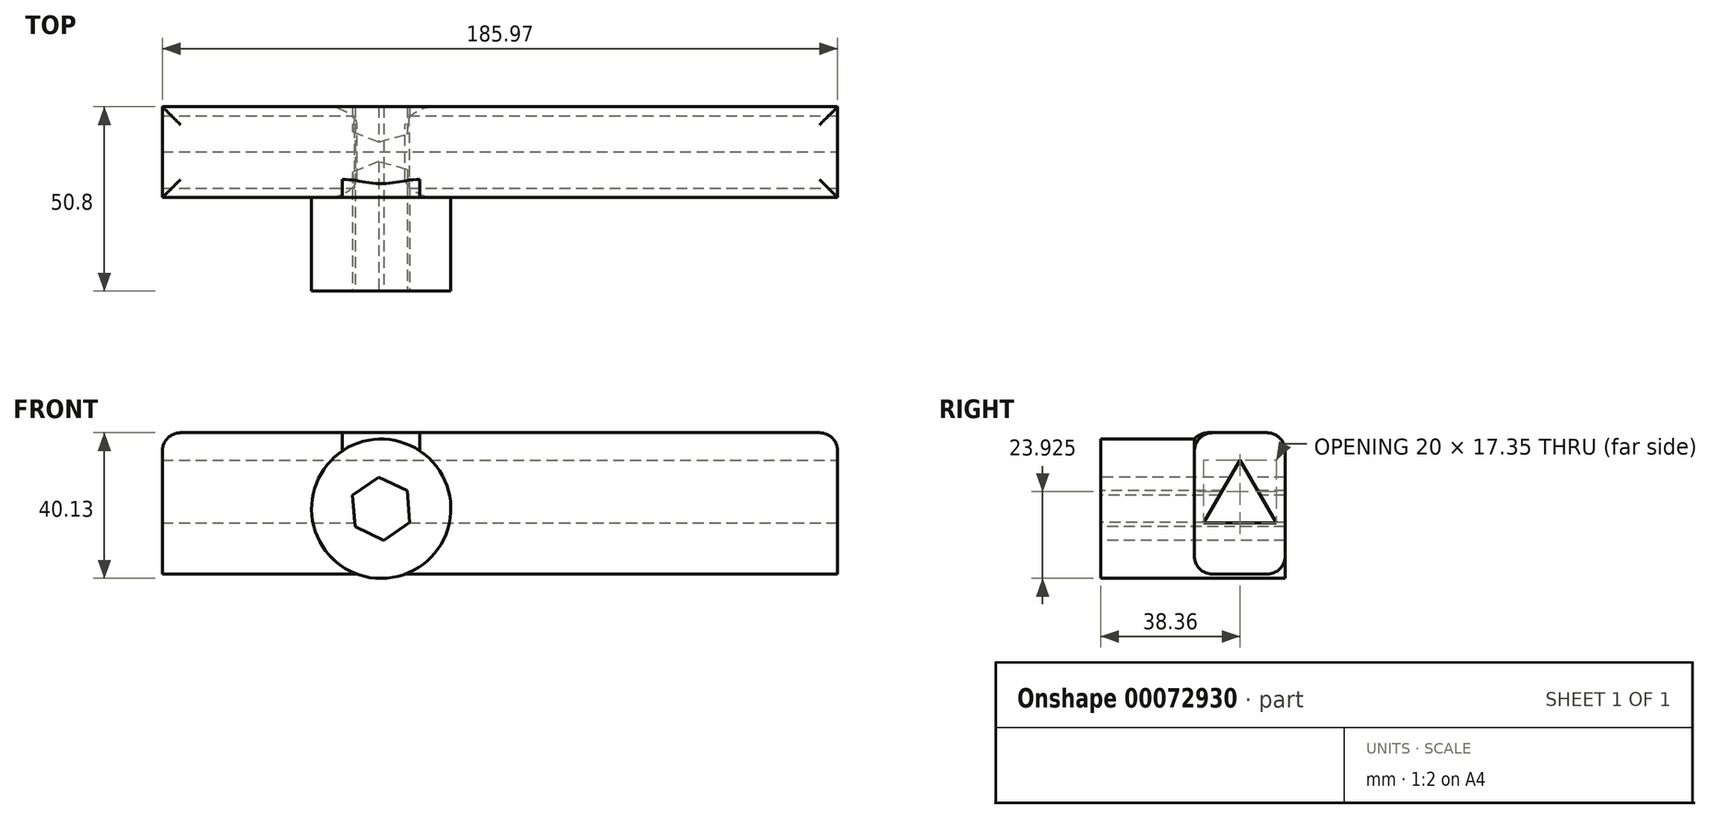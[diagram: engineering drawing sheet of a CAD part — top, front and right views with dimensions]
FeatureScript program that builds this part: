
annotation { "Feature Type Name" : "Feature", "Feature Type Description" : "" }
export const myFeature = defineFeature(function(context is Context, id is Id, definition is map)
    precondition{}
    {
        {
            var Q0;
            Q0=qCreatedBy(makeId("Front.planeOp"),FACE);
            var sketch = newSketch(context, id + "F0", { "sketchPlane" : qUnion([Q0])});
            skCircle(sketch, "E0", {"center": v(-60.55, 49.23) * mm, "radius": 19.19 * mm});
            skSolve(sketch);
        }
        {
            var Q0;
            Q0 = qSketchRegion(id + "F0", true);
            extrude(context, id + "F1", {"entities" : qUnion([Q0]), "depth" : 50.8 * mm});
        }
        {
            var Q0;
            Q0=qCreatedBy(makeId("Front.planeOp"),FACE);
            var sketch = newSketch(context, id + "F2", { "sketchPlane" : qUnion([Q0])});
            skLineSegment(sketch, "E1.bottom", {"start": v(-120.8, 70.18) * mm, "end": v(65.17, 70.18) * mm});
            skLineSegment(sketch, "E1.top", {"start": v(-120.8, 31.22) * mm, "end": v(65.17, 31.22) * mm});
            skLineSegment(sketch, "E1.left", {"start": v(-120.8, 70.18) * mm, "end": v(-120.8, 31.22) * mm});
            skLineSegment(sketch, "E1.right", {"start": v(65.17, 70.18) * mm, "end": v(65.17, 31.22) * mm});
            skSolve(sketch);
        }
        {
            var Q0;
            Q0=makeQuery(id+"F2.imprint","IMPRINT",FACE,{"disambiguationData":[TD([[makeQuery(id+"F2.imprint","IMPRINT",EDGE,{"derivedFrom":sQuery(id+"F2.wireOp",EDGE,"E1.bottom")}),-1.0]])]});
            extrude(context, id + "F3", {"entities" : qUnion([Q0]), "operationType" : NewBodyOperationType.ADD, "depth" : 25 * mm});
        }
        {
            var Q0;
            Q0=makeQuery(id+"F3.opExtrude","SWEPT_FACE",FACE,{"disambiguationData":[OSD([sQuery(id+"F2.wireOp",EDGE,"E1.bottom")])]});
            fillet(context, id + "F4", {"entities" : qUnion([Q0]), "radius" : 5 * mm, "tangentPropagation" : true, "allowEdgeOverflow" : false});
        }
        {
            var Q0;
            {var subQ0=sQuery(id+"F2.wireOp",EDGE,"E1.top");var subQ1=sQuery(id+"F2.wireOp",EDGE,"E1.right");Q0=makeQuery(id+"F3.boolean.opBoolean","SPLIT",EDGE,{"disambiguationData":[TD([makeQuery(id+"F3.opExtrude","SWEPT_FACE",FACE,{"disambiguationData":[OSD([subQ1])]})])],"derivedFrom":makeQuery(id+"F3.opExtrude","CAP_EDGE",EDGE,{"disambiguationData":[OSD([subQ0])],"isStart":true})});}
            fillet(context, id + "F5", {"entities" : qUnion([Q0]), "radius" : 5 * mm, "tangentPropagation" : true, "allowEdgeOverflow" : false});
        }
        {
            var Q0;
            {var subQ0=sQuery(id+"F2.wireOp",EDGE,"E1.top");var subQ1=sQuery(id+"F2.wireOp",EDGE,"E1.left");Q0=makeQuery(id+"F3.boolean.opBoolean","SPLIT",EDGE,{"disambiguationData":[TD([makeQuery(id+"F3.opExtrude","SWEPT_FACE",FACE,{"disambiguationData":[OSD([subQ1])]})])],"derivedFrom":makeQuery(id+"F3.opExtrude","CAP_EDGE",EDGE,{"disambiguationData":[OSD([subQ0])],"isStart":true})});}
            fillet(context, id + "F6", {"entities" : qUnion([Q0]), "radius" : 5 * mm, "tangentPropagation" : true, "allowEdgeOverflow" : false});
        }
        {
            var Q0;
            {var subQ0=sQuery(id+"F2.wireOp",EDGE,"E1.left");var subQ1=sQuery(id+"F2.wireOp",EDGE,"E1.top");Q0=makeQuery(id+"F3.boolean.opBoolean","SPLIT",EDGE,{"disambiguationData":[TD([makeQuery(id+"F3.opExtrude","SWEPT_FACE",FACE,{"disambiguationData":[OSD([subQ0])]})])],"derivedFrom":makeQuery(id+"F3.opExtrude","CAP_EDGE",EDGE,{"disambiguationData":[OSD([subQ1])],"isStart":false})});}
            var Q1;
            {var subQ0=sQuery(id+"F2.wireOp",EDGE,"E1.right");var subQ1=sQuery(id+"F2.wireOp",EDGE,"E1.top");Q1=makeQuery(id+"F3.boolean.opBoolean","SPLIT",EDGE,{"disambiguationData":[TD([makeQuery(id+"F3.opExtrude","SWEPT_FACE",FACE,{"disambiguationData":[OSD([subQ0])]})])],"derivedFrom":makeQuery(id+"F3.opExtrude","CAP_EDGE",EDGE,{"disambiguationData":[OSD([subQ1])],"isStart":false})});}
            fillet(context, id + "F7", {"entities" : qUnion([Q0, Q1]), "radius" : 5 * mm, "tangentPropagation" : true, "allowEdgeOverflow" : false});
        }
        {
            var Q0;
            Q0=makeQuery(id+"F3.opExtrude","SWEPT_FACE",FACE,{"disambiguationData":[OSD([sQuery(id+"F2.wireOp",EDGE,"E1.right")])]});
            var sketch = newSketch(context, id + "F8", { "sketchPlane" : qUnion([Q0])});
            skCircle(sketch, "E2.cCircle", {"center": v(-12.42, 51.1) * mm, "radius": 5.77 * mm, "construction": true});
            skLineSegment(sketch, "E2.0", {"start": v(-2.44, 45.3) * mm, "end": v(-22.44, 45.36) * mm});
            skLineSegment(sketch, "E2.1", {"start": v(-22.44, 45.36) * mm, "end": v(-12.4, 62.65) * mm});
            skLineSegment(sketch, "E2.2", {"start": v(-12.4, 62.65) * mm, "end": v(-2.44, 45.3) * mm});
            skPoint(sketch, "E2.0.midPoint", {"position": v(-12.44, 45.33) * mm});
            skSolve(sketch);
        }
        {
            var Q0;
            Q0=makeQuery(id+"F8.imprint","IMPRINT",FACE,{"disambiguationData":[TD([[makeQuery(id+"F8.imprint","IMPRINT",EDGE,{"derivedFrom":sQuery(id+"F8.wireOp",EDGE,"E2.0")}),-1.0]])]});
            extrude(context, id + "F9", {"entities" : qUnion([Q0]), "operationType" : NewBodyOperationType.REMOVE, "endBound" : BoundingType.THROUGH_ALL, "oppositeDirection" : true, "depth" : 25 * mm});
        }
        {
            var Q0;
            Q0=makeQuery(id+"F1.opExtrude","CAP_FACE",FACE,{"disambiguationData":[OSD([sQuery(id+"F0.wireOp",EDGE,"E0")])],"isStart":false});
            var sketch = newSketch(context, id + "F10", { "sketchPlane" : qUnion([Q0])});
            skCircle(sketch, "E3.cCircle", {"center": v(-60.55, 49.23) * mm, "radius": 7.57 * mm, "construction": true});
            skLineSegment(sketch, "E3.0", {"start": v(-52.66, 45.48) * mm, "end": v(-59.86, 40.52) * mm});
            skLineSegment(sketch, "E3.1", {"start": v(-59.86, 40.52) * mm, "end": v(-67.75, 44.28) * mm});
            skLineSegment(sketch, "E3.2", {"start": v(-67.75, 44.28) * mm, "end": v(-68.44, 52.99) * mm});
            skLineSegment(sketch, "E3.3", {"start": v(-68.44, 52.99) * mm, "end": v(-61.25, 57.95) * mm});
            skLineSegment(sketch, "E3.4", {"start": v(-61.25, 57.95) * mm, "end": v(-53.36, 54.2) * mm});
            skLineSegment(sketch, "E3.5", {"start": v(-53.36, 54.2) * mm, "end": v(-52.66, 45.48) * mm});
            skPoint(sketch, "E3.0.midPoint", {"position": v(-56.26, 43) * mm});
            skSolve(sketch);
        }
        {
            var Q0;
            Q0=makeQuery(id+"F10.imprint","IMPRINT",FACE,{"disambiguationData":[TD([[makeQuery(id+"F10.imprint","IMPRINT",EDGE,{"derivedFrom":sQuery(id+"F10.wireOp",EDGE,"E3.0")}),-1.0]])]});
            extrude(context, id + "F11", {"entities" : qUnion([Q0]), "operationType" : NewBodyOperationType.REMOVE, "endBound" : BoundingType.THROUGH_ALL, "oppositeDirection" : true, "depth" : 25 * mm});
        }
    });
